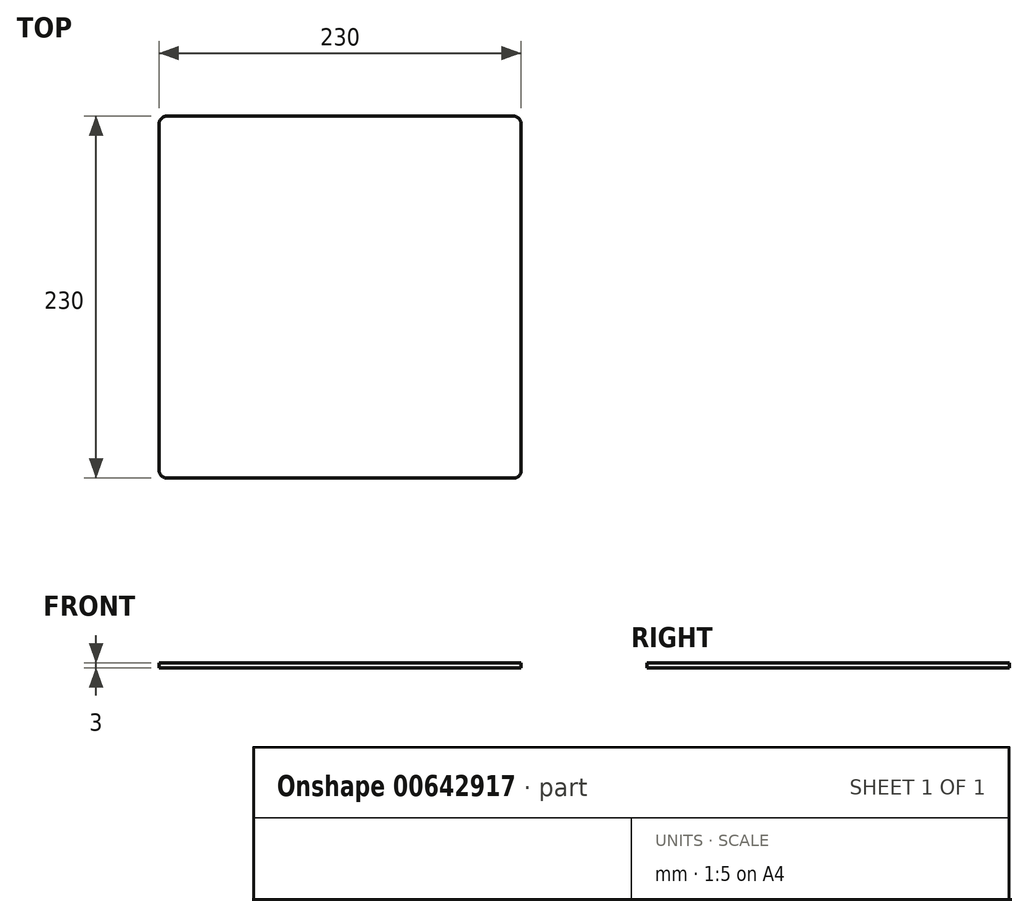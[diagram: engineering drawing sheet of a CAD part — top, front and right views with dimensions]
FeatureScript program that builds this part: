
annotation { "Feature Type Name" : "Feature", "Feature Type Description" : "" }
export const myFeature = defineFeature(function(context is Context, id is Id, definition is map)
    precondition{}
    {
        {
            var Q0;
            Q0=qCreatedBy(makeId("Top.planeOp"),FACE);
            var sketch = newSketch(context, id + "F0", { "sketchPlane" : qUnion([Q0])});
            skLineSegment(sketch, "E0.bottom", {"start": v(115, 115) * mm, "end": v(-115, 115) * mm});
            skLineSegment(sketch, "E0.top", {"start": v(115, -115) * mm, "end": v(-115, -115) * mm});
            skLineSegment(sketch, "E0.left", {"start": v(115, 115) * mm, "end": v(115, -115) * mm});
            skLineSegment(sketch, "E0.right", {"start": v(-115, 115) * mm, "end": v(-115, -115) * mm});
            skPoint(sketch, "E0.middle", {"position": v(0, 0) * mm});
            skSolve(sketch);
        }
        {
            var Q0;
            Q0=makeQuery(id+"F0.imprint","IMPRINT",FACE,{"disambiguationData":[TD([[makeQuery(id+"F0.imprint","IMPRINT",EDGE,{"derivedFrom":sQuery(id+"F0.wireOp",EDGE,"E0.bottom")}),1.0]])]});
            extrude(context, id + "F1", {"entities" : qUnion([Q0]), "depth" : 3 * mm, "offsetDistance" : 25 * mm});
        }
        {
            var Q0;
            Q0=makeQuery(id+"F1.opExtrude","SWEPT_EDGE",EDGE,{"disambiguationData":[OSD([sQuery(id+"F0.wireOp",EDGE,"E0.top"),sQuery(id+"F0.wireOp",EDGE,"E0.right")])]});
            var Q1;
            Q1=makeQuery(id+"F1.opExtrude","SWEPT_EDGE",EDGE,{"disambiguationData":[OSD([sQuery(id+"F0.wireOp",EDGE,"E0.top"),sQuery(id+"F0.wireOp",EDGE,"E0.left")])]});
            var Q2;
            Q2=makeQuery(id+"F1.opExtrude","SWEPT_EDGE",EDGE,{"disambiguationData":[OSD([sQuery(id+"F0.wireOp",EDGE,"E0.bottom"),sQuery(id+"F0.wireOp",EDGE,"E0.left")])]});
            var Q3;
            Q3=makeQuery(id+"F1.opExtrude","SWEPT_EDGE",EDGE,{"disambiguationData":[OSD([sQuery(id+"F0.wireOp",EDGE,"E0.bottom"),sQuery(id+"F0.wireOp",EDGE,"E0.right")])]});
            fillet(context, id + "F2", {"entities" : qUnion([Q0, Q1, Q2, Q3]), "radius" : 5 * mm, "tangentPropagation" : true, "allowEdgeOverflow" : false});
        }
    });
